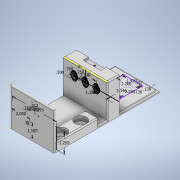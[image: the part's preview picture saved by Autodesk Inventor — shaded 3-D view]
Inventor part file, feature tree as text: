
AUTODESK INVENTOR PART (.ipt)
format: ipt  version: 2020 (Build 240168000, 168)  size: 350,720 bytes
history: native  units: in
note: dims shown in document units (in); Inventor stores cm internally (conversion verified against a paired STEP export)
features: sketch x12, extrude x11, hole x4, fillet x2
ambient origin geometry x8: Origin, YZ Plane, XZ Plane, XY Plane, X Axis, Y Axis, Z Axis, Center Point
bodies: Solid1 (feature_tree)
feature tree (29):
  extrude  "Extrusion1"  Depth=4.0in
  sketch  "Sketch2"  dims[d2=1.375in d3=0.0in d4=1.25in]
  extrude  "Extrusion2"  Depth=1.25in
  extrude  "Extrusion3"  Depth=2.5in
  extrude  "Extrusion4"  Depth=0.78in
  extrude  "Extrusion5"  Depth=0.25in
  sketch  "Sketch5"  dims[d10=1.25in d11=0.0in d12=0.25in]
  hole  "Hole1"  [1 undecoded]
  extrude  "Extrusion9"  Depth=5.0in
  extrude  "Extrusion10"  Depth=6.0in TaperAngle=0.0deg
  extrude  "Extrusion11"  Depth=4.0in TaperAngle=0.0deg
  sketch  "Sketch13"  dims[d24=0.25in d25=6.0in d26=0.0in]
  extrude  "Extrusion12"  Depth=2.25in
  hole  "Hole2"  [1 undecoded]
  extrude  "Extrusion13"  Depth=0.125in
  extrude  "Extrusion14"  Depth=0.125in
  hole  "Hole3"  [1 undecoded]
  fillet  "Fillet1"  Radius=1.5in
  fillet  "Fillet2"  Radius=5.0in
  sketch  "Sketch17"  dims[d34=0.356in d35=0.333in d36=0.712in d37=0.134in d38=0.75in d39=0.256in d40=0.118in d41=0.5635in d42=1.0in d43=0.8108in d58=1.0in d59=1.5in d60=5.0in d61=0.75in d62=0.0in d69=1.3in d70=1.3in d71=0.5in d72=0.0in d73=4.5in d74=0.0in d75=3.3465in d76=2.2047in d77=0.1378in d78=0.1378in d79=0.1575in d80=0.7874in d82=1.9291in d83=0.7874in d85=2.2835in d88=0.125in d89=0.0in d90=0.0793in d91=0.197in d92=0.217in d93=0.098in d94=0.5635in d95=0.299in d96=0.8108in d97=0.2in d98=5.0in d99=0.2in d100=0.2in d101=0.125in d102=0.0in d103=0.3in d104=2.0in d105=0.2in d106=0.0in d107=0.196in d108=0.25in d109=0.217in d110=0.098in d111=0.5635in d112=0.25in d113=0.8108in d114=0.125in d115=1.25in d116=90.0deg d117=1.25in d118=90.0deg d119=0.125in d120=2.0in d121=1.5in d122=0.35in d123=0.75in d124=0.375in d125=0.25in d126=0.5635in d127=0.5in d128=0.0in]
  hole  "Hole4"  [1 undecoded]
  sketch  "Sketch1"  dims[d0=5.0in d1=4.0in]
  sketch  "Sketch3"  dims[d5=1.25in d6=2.5in]
  sketch  "Sketch4"  dims[d7=0.78in d9=0.78in]
  sketch  "Sketch10"  dims[d13=0.5in d14=1.1811in d16=1.25in d17=0.3937in d19=1.0in]
  sketch  "Sketch12"  dims[d21=0.0in d22=0.0in d23=5.0in]
  sketch  "Sketch14"  dims[d27=0.25in d28=4.0in d29=0.0in]
  sketch  "Sketch15"  dims[d30=5.0in d31=2.25in]
  sketch  "Sketch16"  dims[d32=1.293in d33=90.0deg]
note: 4 required parameter values undecoded (feature->parameter linkage not recoverable at this tier; creation-order binding heuristic only, values carry confidence <= 0.55)
